# Revit family: 928-10-001 DN50-500
name_source: partatom
category: Pipe Accessories
units: mm (PartAtom-declared; Revit-internal decimal feet)

## family parameters
Always vertical = Yes
Cut with Voids When Loaded = No
Part Type = Valve - Breaks Into
Round Connector Dimension = Use Diameter
Shared = No
Work Plane-Based = No

## types (11) — shared parameters
4 = 4 mm  [stored 0.0131234 ft]
DN050_PN10/16 = 928-050-10-020010200
DN080_PN10/16 = 928-080-10-020010200
DN100_PN10/16 = 928-100-10-020010200
DN150_PN10/16 = 928-150-10-020010200
DN200_PN10/16 = 928-200-10-020010200
DN250_PN10/16 = 928-250-10-020010200
DN300_PN10/16 = 928-300-10-020010200
DN350_PN10/16 = 928-350-10-020010200
DN400_PN10/16 = 928-400-10-020010200
DN450_PN10/16 = 928-450-10-020010200
DN500_PN10/16 = 928-500-10-020010200
Description_ = AVK BUTTERFLY VALVE, WAFER, PN10/16
Search_table = 928-10-001 DN50-500
URL_product_pages = https://www.avkvalves.com
zero-valued in all types: Default Elevation

## per-type parameters (varying)
| type | A | B | Bore | Bore1 | Bore2 | Cut2 | Cut3 | DN | Hole_R | Hole_R_location | Hole_location | Hook | Length | Rib_T | Thickness_Body | cut | hole_location2 | inside_rib | length_dis | retainer | retainer1 | retainer_start |
| DN050_PN10/16 | 91 mm | 54 mm | 25 mm  [stored 0.082021 ft] | 23 mm  [stored 0.0754593 ft] | 4 mm  [stored 0.0131234 ft] | 46 mm  [stored 0.150919 ft] | 1 mm  [stored 0.00328084 ft] | 50 mm | 2 mm  [stored 0.00656168 ft] | 3 mm  [stored 0.00984252 ft] | 7 mm  [stored 0.0229659 ft] | 6 mm  [stored 0.019685 ft] | 1 mm  [stored 0.00328084 ft] | 6 mm  [stored 0.019685 ft] | 6 mm  [stored 0.019685 ft] | 4 mm  [stored 0.0131234 ft] | 4 mm  [stored 0.0131234 ft] | 23 mm  [stored 0.0754593 ft] | 22 mm  [stored 0.0721785 ft] | 2 mm  [stored 0.00656168 ft] | 21 mm | 10 mm  [stored 0.0328084 ft] |
| DN080_PN10/16 | 142 mm | 77 mm | 40 mm  [stored 0.131234 ft] | 37 mm  [stored 0.121391 ft] | 6 mm  [stored 0.019685 ft] | 72 mm | 2 mm  [stored 0.00656168 ft] | 80 mm | 2 mm  [stored 0.00656168 ft] | 3 mm  [stored 0.00984252 ft] | 7 mm  [stored 0.0229659 ft] | 6 mm  [stored 0.019685 ft] | 2 mm  [stored 0.00656168 ft] | 6 mm  [stored 0.019685 ft] | 6 mm  [stored 0.019685 ft] | 6 mm  [stored 0.019685 ft] | 4 mm  [stored 0.0131234 ft] | 36 mm  [stored 0.11811 ft] | 31 mm  [stored 0.101706 ft] | 3 mm  [stored 0.00984252 ft] | 31 mm  [stored 0.101706 ft] | 16 mm  [stored 0.0524934 ft] |
| DN100_PN10/16 | 174 mm | 97 mm | 50 mm | 47 mm  [stored 0.154199 ft] | 8 mm  [stored 0.0262467 ft] | 88 mm | 2 mm  [stored 0.00656168 ft] | 100 mm | 2 mm  [stored 0.00656168 ft] | 3 mm  [stored 0.00984252 ft] | 9 mm  [stored 0.0295276 ft] | 7 mm  [stored 0.0229659 ft] | 2 mm  [stored 0.00656168 ft] | 7 mm  [stored 0.0229659 ft] | 7 mm  [stored 0.0229659 ft] | 6 mm  [stored 0.019685 ft] | 5 mm  [stored 0.0164042 ft] | 45 mm  [stored 0.147638 ft] | 39 mm | 3 mm  [stored 0.00984252 ft] | 37 mm  [stored 0.121391 ft] | 19 mm |
| DN150_PN10/16 | 246 mm | 147 mm | 75 mm | 70 mm | 11 mm  [stored 0.0360892 ft] | 125 mm | 3 mm  [stored 0.00984252 ft] | 150 mm | 3 mm  [stored 0.00984252 ft] | 5 mm  [stored 0.0164042 ft] | 9 mm  [stored 0.0295276 ft] | 7 mm  [stored 0.0229659 ft] | 2 mm  [stored 0.00656168 ft] | 7 mm  [stored 0.0229659 ft] | 7 mm  [stored 0.0229659 ft] | 6 mm  [stored 0.019685 ft] | 5 mm  [stored 0.0164042 ft] | 68 mm | 59 mm | 3 mm  [stored 0.00984252 ft] | 48 mm  [stored 0.15748 ft] | 24 mm  [stored 0.0787402 ft] |
| DN200_PN10/16 | 290 mm | 124 mm | 100 mm | 93 mm | 15 mm  [stored 0.0492126 ft] | 147 mm | 4 mm  [stored 0.0131234 ft] | 200 mm | 3 mm  [stored 0.00984252 ft] | 5 mm  [stored 0.0164042 ft] | 11 mm  [stored 0.0360892 ft] | 8 mm  [stored 0.0262467 ft] | 3 mm  [stored 0.00984252 ft] | 8 mm  [stored 0.0262467 ft] | 8 mm  [stored 0.0262467 ft] | 6 mm  [stored 0.019685 ft] | 6 mm  [stored 0.019685 ft] | 90 mm | 50 mm | 3 mm  [stored 0.00984252 ft] | 45 mm  [stored 0.147638 ft] | 23 mm  [stored 0.0754593 ft] |
| DN250_PN10/16 | 352 mm | 142 mm | 125 mm | 116 mm | 19 mm | 178 mm | 4 mm  [stored 0.0131234 ft] | 250 mm | 3 mm  [stored 0.00984252 ft] | 5 mm  [stored 0.0164042 ft] | 13 mm | 8 mm  [stored 0.0262467 ft] | 3 mm  [stored 0.00984252 ft] | 8 mm  [stored 0.0262467 ft] | 8 mm  [stored 0.0262467 ft] | 8 mm  [stored 0.0262467 ft] | 7 mm  [stored 0.0229659 ft] | 113 mm | 57 mm | 4 mm  [stored 0.0131234 ft] | 51 mm | 26 mm |
| DN300_PN10/16 | 398 mm | 177 mm | 150 mm | 140 mm | 23 mm  [stored 0.0754593 ft] | 202 mm | 4 mm  [stored 0.0131234 ft] | 300 mm | 4 mm  [stored 0.0131234 ft] | 6 mm  [stored 0.019685 ft] | 16 mm  [stored 0.0524934 ft] | 8 mm  [stored 0.0262467 ft] | 3 mm  [stored 0.00984252 ft] | 8 mm  [stored 0.0262467 ft] | 9 mm  [stored 0.0295276 ft] | 8 mm  [stored 0.0262467 ft] | 8 mm  [stored 0.0262467 ft] | 135 mm | 71 mm | 4 mm  [stored 0.0131234 ft] | 49 mm | 25 mm  [stored 0.082021 ft] |
| DN350_PN10/16 | 460 mm | 218 mm | 175 mm | 163 mm | 26 mm | 231 mm | 4 mm  [stored 0.0131234 ft] | 350 mm | 4 mm  [stored 0.0131234 ft] | 6 mm  [stored 0.019685 ft] | 18 mm  [stored 0.0590551 ft] | 12 mm  [stored 0.0393701 ft] | 4 mm  [stored 0.0131234 ft] | 8 mm  [stored 0.0262467 ft] | 9 mm  [stored 0.0295276 ft] | 8 mm  [stored 0.0262467 ft] | 9 mm  [stored 0.0295276 ft] | 158 mm | 87 mm | 4 mm  [stored 0.0131234 ft] | 55 mm | 28 mm |
| DN400_PN10/16 | 520 mm | 228 mm | 200 mm | 186 mm | 30 mm  [stored 0.0984252 ft] | 264 mm | 6 mm  [stored 0.019685 ft] | 400 mm | 5 mm  [stored 0.0164042 ft] | 8 mm  [stored 0.0262467 ft] | 20 mm  [stored 0.0656168 ft] | 13 mm | 4 mm  [stored 0.0131234 ft] | 9 mm  [stored 0.0295276 ft] | 10 mm  [stored 0.0328084 ft] | 8 mm  [stored 0.0262467 ft] | 10 mm  [stored 0.0328084 ft] | 180 mm | 91 mm | 4 mm  [stored 0.0131234 ft] | 60 mm | 30 mm  [stored 0.0984252 ft] |
| DN450_PN10/16 | 554 mm | 256 mm | 225 mm | 209 mm | 34 mm | 280 mm | 6 mm  [stored 0.019685 ft] | 450 mm | 5 mm  [stored 0.0164042 ft] | 8 mm  [stored 0.0262467 ft] | 22 mm  [stored 0.0721785 ft] | 14 mm  [stored 0.0459318 ft] | 5 mm  [stored 0.0164042 ft] | 9 mm  [stored 0.0295276 ft] | 10 mm  [stored 0.0328084 ft] | 8 mm  [stored 0.0262467 ft] | 11 mm  [stored 0.0360892 ft] | 203 mm | 102 mm | 4 mm  [stored 0.0131234 ft] | 52 mm | 26 mm |
| DN500_PN10/16 | 626 mm | 288 mm | 250 mm | 233 mm | 38 mm | 316 mm | 6 mm  [stored 0.019685 ft] | 500 mm | 5 mm  [stored 0.0164042 ft] | 8 mm  [stored 0.0262467 ft] | 24 mm  [stored 0.0787402 ft] | 15 mm  [stored 0.0492126 ft] | 5 mm  [stored 0.0164042 ft] | 9 mm  [stored 0.0295276 ft] | 10 mm  [stored 0.0328084 ft] | 8 mm  [stored 0.0262467 ft] | 12 mm  [stored 0.0393701 ft] | 225 mm | 115 mm | 4 mm  [stored 0.0131234 ft] | 63 mm | 32 mm |

note: [stored X ft] marks values corroborated as IEEE doubles in the binary element streams (Revit-internal decimal feet)

## geometry (parser evidence)
native form markers: Sweep x6
no freeform markers — native parametric forms only
